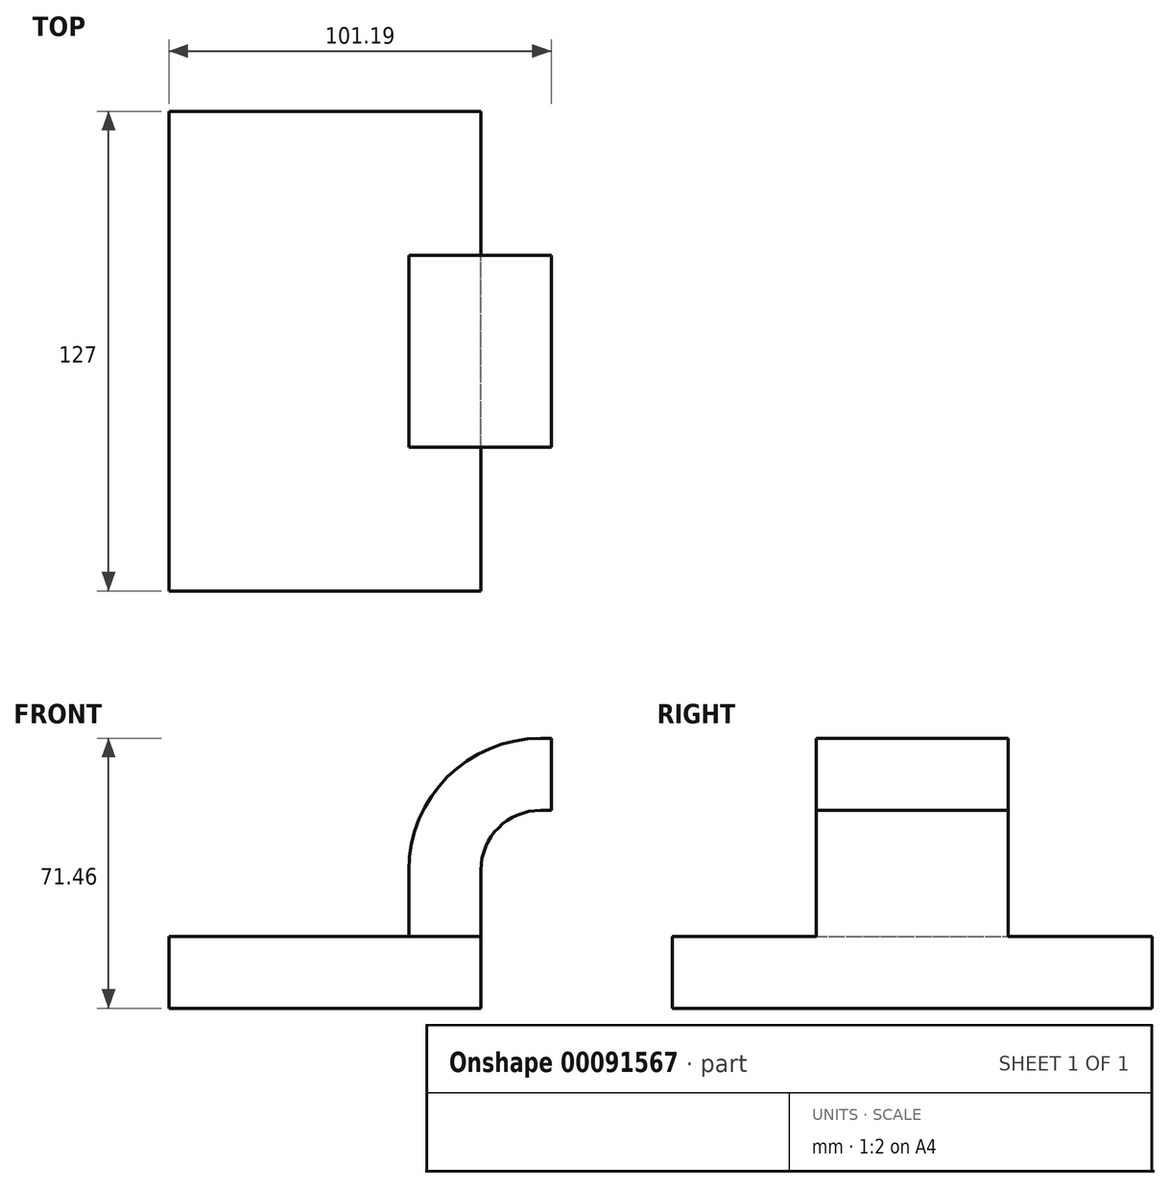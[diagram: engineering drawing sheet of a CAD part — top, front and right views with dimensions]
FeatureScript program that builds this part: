
annotation { "Feature Type Name" : "Feature", "Feature Type Description" : "" }
export const myFeature = defineFeature(function(context is Context, id is Id, definition is map)
    precondition{}
    {
        {
            var Q0;
            Q0=qCreatedBy(makeId("Front.planeOp"),FACE);
            var sketch = newSketch(context, id + "F0", { "sketchPlane" : qUnion([Q0])});
            skLineSegment(sketch, "E0.bottom", {"start": v(41.27, 9.53) * mm, "end": v(-41.28, 9.53) * mm});
            skLineSegment(sketch, "E0.top", {"start": v(41.28, -9.52) * mm, "end": v(-41.27, -9.52) * mm});
            skLineSegment(sketch, "E0.left", {"start": v(41.27, 9.53) * mm, "end": v(41.28, -9.52) * mm});
            skLineSegment(sketch, "E0.right", {"start": v(-41.28, 9.53) * mm, "end": v(-41.27, -9.52) * mm});
            skPoint(sketch, "E0.middle", {"position": v(0, 0) * mm});
            skLineSegment(sketch, "E1.bottom", {"start": v(59.91, 38.1) * mm, "end": v(110.71, 38.1) * mm});
            skLineSegment(sketch, "E1.top", {"start": v(59.91, 66.68) * mm, "end": v(110.71, 66.68) * mm});
            skLineSegment(sketch, "E1.left", {"start": v(59.91, 38.1) * mm, "end": v(59.91, 66.67) * mm});
            skLineSegment(sketch, "E1.right", {"start": v(110.71, 38.1) * mm, "end": v(110.71, 66.67) * mm});
            skPoint(sketch, "E1.middle", {"position": v(85.31, 52.39) * mm});
            skLineSegment(sketch, "E2", {"start": v(41.27, 9.53) * mm, "end": v(41.27, 27) * mm});
            skArc(sketch, "E3", {"start": v(41.27, 27) * mm, "mid": v(45.92, 38.23) * mm, "end": v(57.15, 42.88) * mm});
            skLineSegment(sketch, "E4", {"start": v(57.15, 42.88) * mm, "end": v(85.72, 42.88) * mm});
            skLineSegment(sketch, "E5.0", {"start": v(57.15, 61.93) * mm, "end": v(85.38, 61.93) * mm});
            skArc(sketch, "E5.1", {"start": v(22.22, 27) * mm, "mid": v(32.45, 51.7) * mm, "end": v(57.15, 61.93) * mm});
            skLineSegment(sketch, "E5.2", {"start": v(22.22, 9.53) * mm, "end": v(22.22, 27) * mm});
            skFitSpline(sketch, "E6", {"points": [v(-41.28, 9.52) * mm, v(57.15, 61.93) * mm], "startDerivative": vector(0.76, 82.78) * mm, "endDerivative": vector(132.43, -2.42) * mm});
            skLineSegment(sketch, "E7", {"start": v(85.31, 66.68) * mm, "end": v(85.72, 38.1) * mm});
            skSolve(sketch);
        }
        {
            var Q0;
            Q0=makeQuery(id+"F0.imprint","IMPRINT",FACE,{"disambiguationData":[TD([[makeQuery(id+"F0.imprint","IMPRINT",EDGE,{"derivedFrom":sQuery(id+"F0.wireOp",EDGE,"E0.top")}),-1.0]])]});
            extrude(context, id + "F1", {"entities" : qUnion([Q0]), "endBound" : BoundingType.SYMMETRIC, "depth" : 127 * mm});
        }
        {
            var Q0;
            {var subQ2=sQuery(id+"F0.wireOp",EDGE,"E2");Q0=makeQuery(id+"F0.imprint","IMPRINT",FACE,{"disambiguationData":[TD([[makeQuery(id+"F0.imprint","IMPRINT",EDGE,{"derivedFrom":subQ2}),1.0]])]});}
            extrude(context, id + "F2", {"entities" : qUnion([Q0]), "operationType" : NewBodyOperationType.ADD, "endBound" : BoundingType.SYMMETRIC, "depth" : 50.8 * mm});
        }
        {
            var Q0;
            Q0=makeQuery(id+"F0.imprint","IMPRINT",FACE,{"disambiguationData":[TD([[makeQuery(id+"F0.imprint","IMPRINT",EDGE,{"derivedFrom":sQuery(id+"F0.wireOp",EDGE,"E5.1")}),1.0]])]});
            extrude(context, id + "F3", {"entities" : qUnion([Q0]), "operationType" : NewBodyOperationType.ADD, "endBound" : BoundingType.SYMMETRIC, "depth" : 25.4 * mm});
        }
    });
